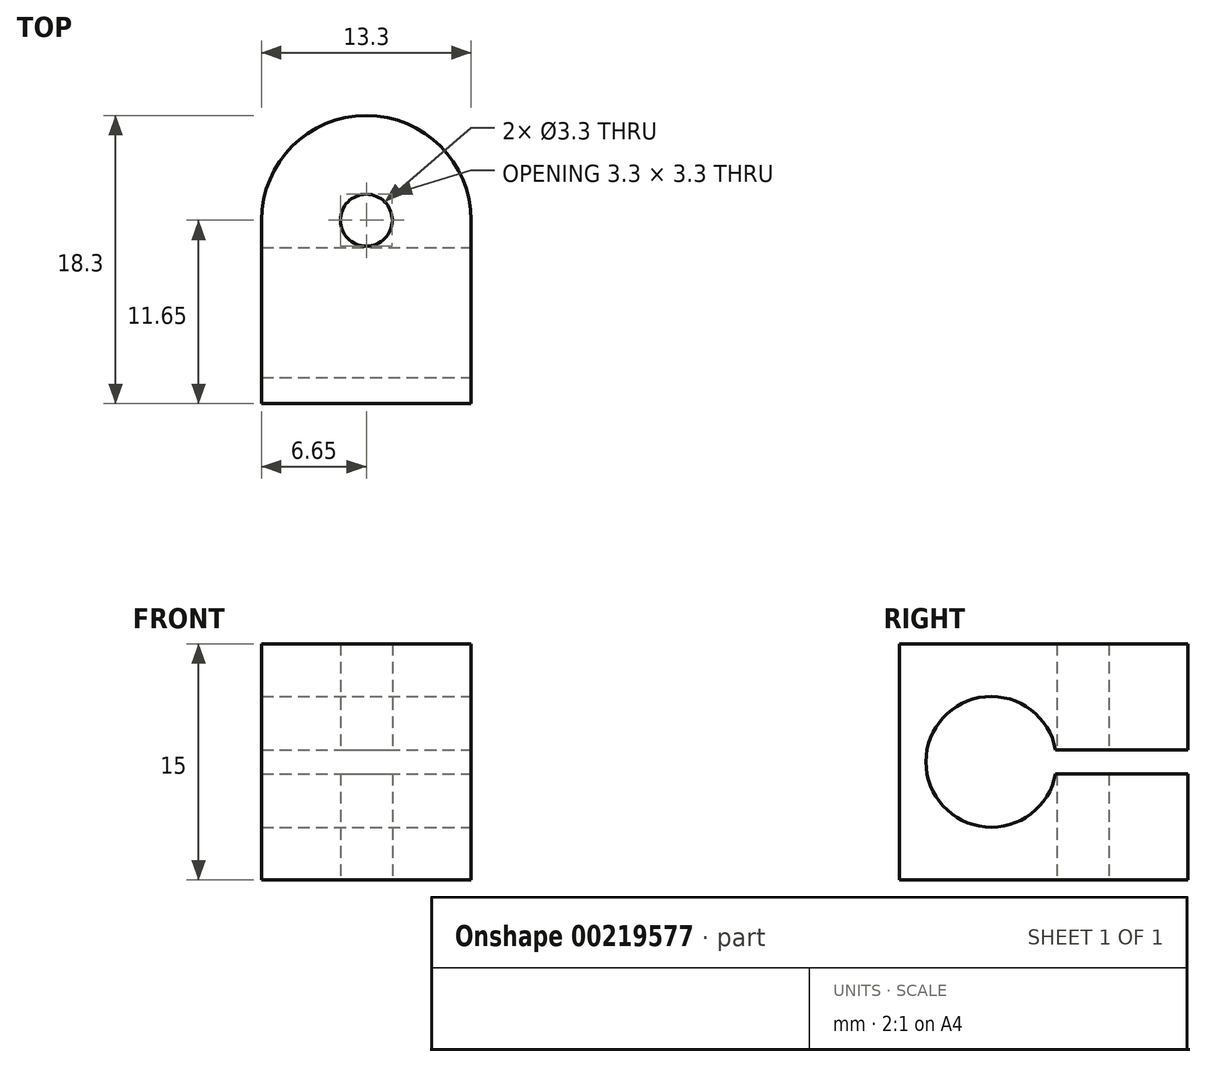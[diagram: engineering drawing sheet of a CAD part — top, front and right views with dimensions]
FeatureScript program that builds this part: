
annotation { "Feature Type Name" : "Feature", "Feature Type Description" : "" }
export const myFeature = defineFeature(function(context is Context, id is Id, definition is map)
    precondition{}
    {
        {
            var Q0;
            Q0=qCreatedBy(makeId("Top.planeOp"),FACE);
            var sketch = newSketch(context, id + "F0", { "sketchPlane" : qUnion([Q0])});
            skCircle(sketch, "E0", {"center": v(0, 0) * mm, "radius": 1.65 * mm});
            skCircle(sketch, "E1", {"center": v(0, 0) * mm, "radius": 6.65 * mm});
            skLineSegment(sketch, "E2.bottom", {"start": v(-6.65, 0) * mm, "end": v(6.65, 0) * mm});
            skLineSegment(sketch, "E2.top", {"start": v(-6.65, -11.65) * mm, "end": v(6.65, -11.65) * mm});
            skLineSegment(sketch, "E2.left", {"start": v(-6.65, 0) * mm, "end": v(-6.65, -11.65) * mm});
            skLineSegment(sketch, "E2.right", {"start": v(6.65, 0) * mm, "end": v(6.65, -11.65) * mm});
            skSolve(sketch);
        }
        {
            var Q0;
            Q0=qSketchRegion(id+"F0",true);
            extrude(context, id + "F1", {"entities" : qUnion([Q0]), "depth" : 15 * mm});
        }
        {
            var Q0;
            Q0=makeQuery(id+"F1.opExtrude","SWEPT_FACE",FACE,{"disambiguationData":[OSD([sQuery(id+"F0.wireOp",EDGE,"E2.right")])]});
            var sketch = newSketch(context, id + "F2", { "sketchPlane" : qUnion([Q0])});
            skCircle(sketch, "E3", {"center": v(-5.83, 7.5) * mm, "radius": 4.15 * mm});
            skPoint(sketch, "E3.centerSnap0", {"position": v(-5.83, 0) * mm});
            skPoint(sketch, "E3.centerSnap1", {"position": v(-11.65, 7.5) * mm});
            skLineSegment(sketch, "E4.bottom", {"start": v(-1.74, 6.75) * mm, "end": v(9.37, 6.75) * mm});
            skLineSegment(sketch, "E4.top", {"start": v(-1.74, 8.25) * mm, "end": v(9.37, 8.25) * mm});
            skLineSegment(sketch, "E4.left", {"start": v(-1.74, 6.75) * mm, "end": v(-1.74, 8.25) * mm});
            skLineSegment(sketch, "E4.right", {"start": v(9.37, 6.75) * mm, "end": v(9.37, 8.25) * mm});
            skSolve(sketch);
        }
        {
            var Q0;
            Q0 = qSketchRegion(id + "F2", true);
            extrude(context, id + "F3", {"entities" : qUnion([Q0]), "operationType" : NewBodyOperationType.REMOVE, "endBound" : BoundingType.UP_TO_NEXT, "oppositeDirection" : true, "depth" : 25 * mm, "offsetDistance" : 25 * mm});
        }
    });
